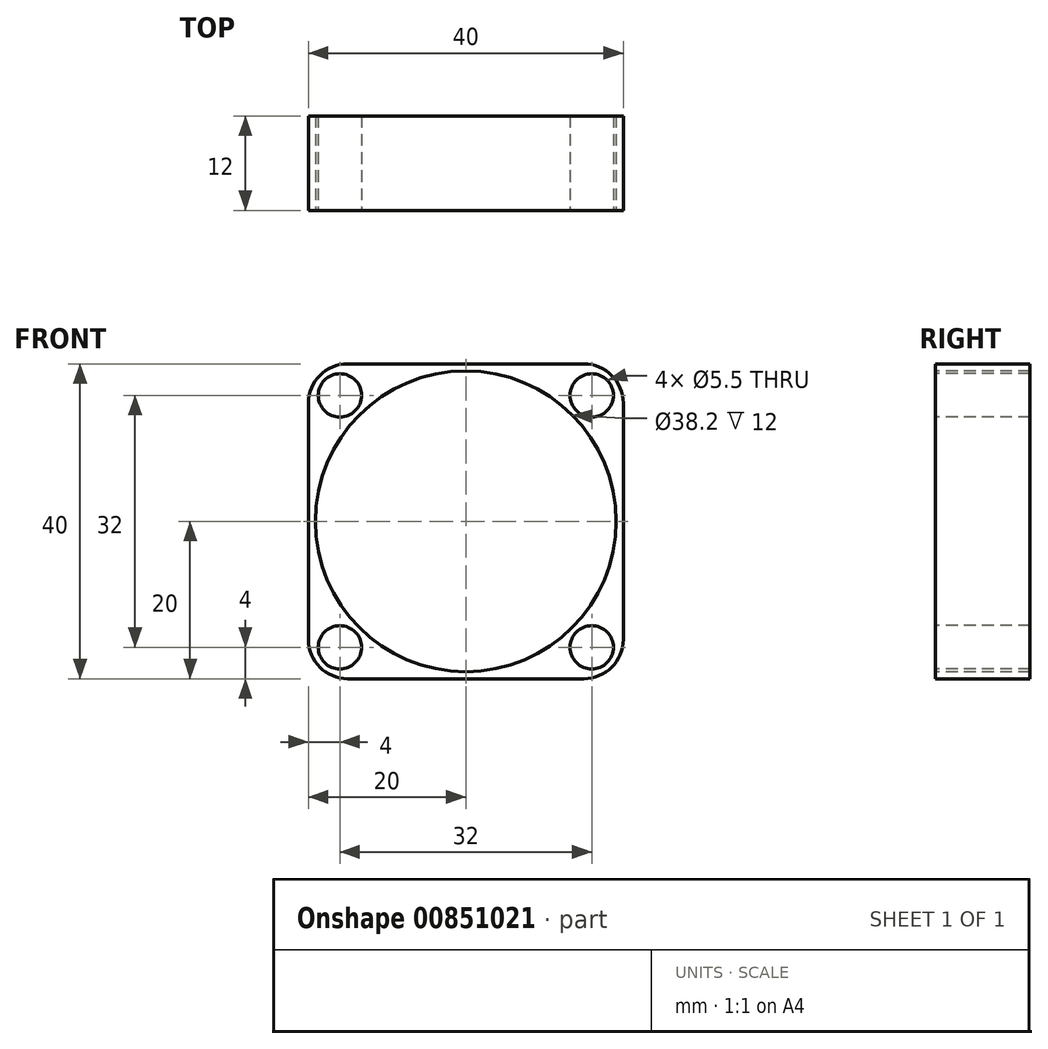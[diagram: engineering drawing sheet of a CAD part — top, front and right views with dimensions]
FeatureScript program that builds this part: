
annotation { "Feature Type Name" : "Feature", "Feature Type Description" : "" }
export const myFeature = defineFeature(function(context is Context, id is Id, definition is map)
    precondition{}
    {
        {
            var Q0;
            Q0=qCreatedBy(makeId("Front.planeOp"),FACE);
            var sketch = newSketch(context, id + "F0", { "sketchPlane" : qUnion([Q0])});
            skPoint(sketch, "E0.middle", {"position": v(0, 0) * mm});
            skLineSegment(sketch, "E1.bottom", {"start": v(-15, 20) * mm, "end": v(15, 20) * mm});
            skLineSegment(sketch, "E1.top", {"start": v(-15, -20) * mm, "end": v(15, -20) * mm});
            skLineSegment(sketch, "E1.left", {"start": v(-20, 15) * mm, "end": v(-20, -15) * mm});
            skLineSegment(sketch, "E1.right", {"start": v(20, 15) * mm, "end": v(20, -15) * mm});
            skCircle(sketch, "E2", {"center": v(0, 0) * mm, "radius": 19.1 * mm});
            skCircle(sketch, "E3", {"center": v(-16, -16) * mm, "radius": 2.75 * mm});
            skLineSegment(sketch, "E4", {"start": v(0, 0) * mm, "end": v(0, -20) * mm, "construction": true});
            skLineSegment(sketch, "E5", {"start": v(0, 0) * mm, "end": v(-20, 0) * mm, "construction": true});
            skCircle(sketch, "E6.MirrorC", {"center": v(16, -16) * mm, "radius": 2.75 * mm});
            skCircle(sketch, "E7.MirrorC", {"center": v(-16, 16) * mm, "radius": 2.75 * mm});
            skCircle(sketch, "E8.MirrorC", {"center": v(16, 16) * mm, "radius": 2.75 * mm});
            skPoint(sketch, "E9.visualSharp", {"position": v(-20, 20) * mm});
            skArc(sketch, "E9.filletArc", {"start": v(-15, 20) * mm, "mid": v(-18.54, 18.54) * mm, "end": v(-20, 15) * mm});
            skPoint(sketch, "E10.visualSharp", {"position": v(20, 20) * mm});
            skArc(sketch, "E10.filletArc", {"start": v(20, 15) * mm, "mid": v(18.54, 18.54) * mm, "end": v(15, 20) * mm});
            skPoint(sketch, "E11.visualSharp", {"position": v(20, -20) * mm});
            skArc(sketch, "E11.filletArc", {"start": v(15, -20) * mm, "mid": v(18.54, -18.54) * mm, "end": v(20, -15) * mm});
            skPoint(sketch, "E12.visualSharp", {"position": v(-20, -20) * mm});
            skArc(sketch, "E12.filletArc", {"start": v(-20, -15) * mm, "mid": v(-18.54, -18.54) * mm, "end": v(-15, -20) * mm});
            skSolve(sketch);
        }
        {
            var Q0;
            Q0=makeQuery(id+"F0.imprint","IMPRINT",FACE,{"disambiguationData":[TD([[makeQuery(id+"F0.imprint","IMPRINT",EDGE,{"derivedFrom":sQuery(id+"F0.wireOp",EDGE,"E1.bottom")}),-1.0]])]});
            extrude(context, id + "F1", {"entities" : qUnion([Q0]), "oppositeDirection" : true, "depth" : 12 * mm, "offsetDistance" : 25 * mm});
        }
    });
